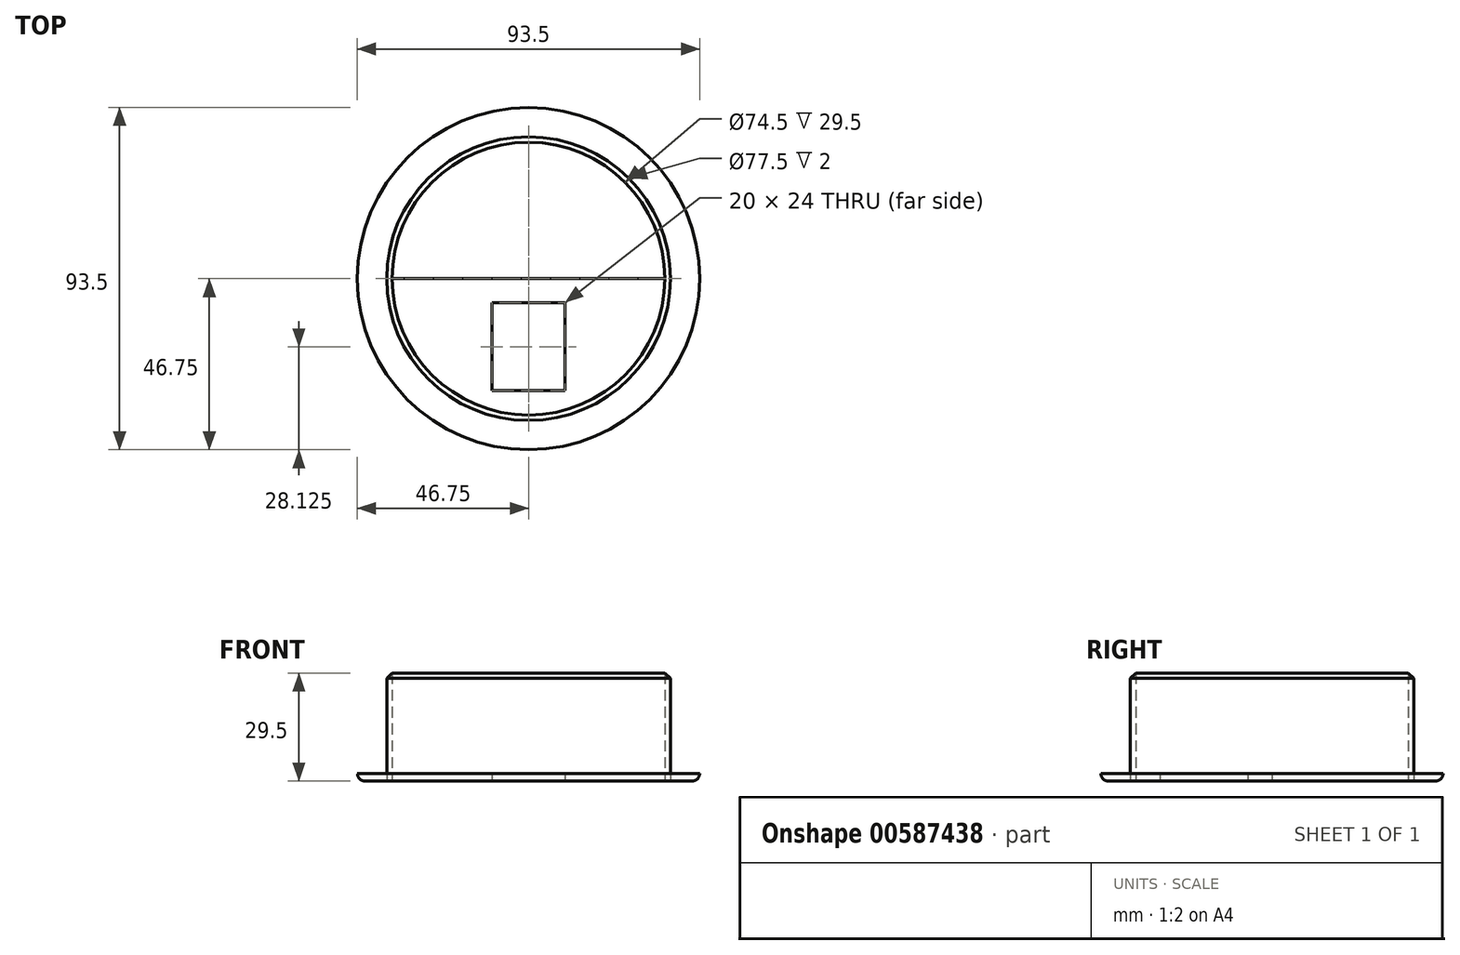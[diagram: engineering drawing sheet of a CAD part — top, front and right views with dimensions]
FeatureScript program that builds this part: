
annotation { "Feature Type Name" : "Feature", "Feature Type Description" : "" }
export const myFeature = defineFeature(function(context is Context, id is Id, definition is map)
    precondition{}
    {
        {
            var Q0;
            Q0=qCreatedBy(makeId("Top.planeOp"),FACE);
            var sketch = newSketch(context, id + "F0", { "sketchPlane" : qUnion([Q0])});
            skCircle(sketch, "E0", {"center": v(0, 0) * mm, "radius": 46.75 * mm});
            skCircle(sketch, "E1", {"center": v(0, 0) * mm, "radius": 38.75 * mm});
            skCircle(sketch, "E2", {"center": v(0, 0) * mm, "radius": 37.25 * mm});
            skLineSegment(sketch, "E3", {"start": v(37.25, 0) * mm, "end": v(38.75, 0) * mm, "construction": true});
            skLineSegment(sketch, "E4", {"start": v(38.75, 0) * mm, "end": v(46.75, 0) * mm, "construction": true});
            skLineSegment(sketch, "E5", {"start": v(-37.25, 0) * mm, "end": v(37.25, 0) * mm});
            skLineSegment(sketch, "E6.bottom", {"start": v(-10, -6.62) * mm, "end": v(10, -6.62) * mm});
            skLineSegment(sketch, "E6.top", {"start": v(-10, -30.62) * mm, "end": v(10, -30.62) * mm});
            skLineSegment(sketch, "E6.left", {"start": v(-10, -6.63) * mm, "end": v(-10, -30.62) * mm});
            skLineSegment(sketch, "E6.right", {"start": v(10, -6.63) * mm, "end": v(10, -30.62) * mm});
            skLineSegment(sketch, "E7", {"start": v(0, -30.62) * mm, "end": v(0, -6.63) * mm, "construction": true});
            skPoint(sketch, "E8", {"position": v(0, -18.62) * mm});
            skLineSegment(sketch, "E9", {"start": v(0, 0) * mm, "end": v(0, -37.25) * mm, "construction": true});
            skSolve(sketch);
        }
        {
            var Q0;
            Q0=makeQuery(id+"F0.imprint","IMPRINT",FACE,{"disambiguationData":[TD([[makeQuery(id+"F0.imprint","IMPRINT",EDGE,{"derivedFrom":sQuery(id+"F0.wireOp",EDGE,"E0")}),1.0]])]});
            var Q1;
            {var subQ0=sQuery(id+"F0.wireOp",EDGE,"E5");Q1=makeQuery(id+"F0.imprint","IMPRINT",FACE,{"disambiguationData":[TD([[makeQuery(id+"F0.imprint","IMPRINT",EDGE,{"derivedFrom":subQ0}),-1.0]])]});}
            extrude(context, id + "F1", {"entities" : qUnion([Q0, Q1]), "depth" : 2 * mm, "offsetDistance" : 25 * mm});
        }
        {
            var Q0;
            Q0=makeQuery(id+"F0.imprint","IMPRINT",FACE,{"disambiguationData":[TD([[makeQuery(id+"F0.imprint","IMPRINT",EDGE,{"derivedFrom":sQuery(id+"F0.wireOp",EDGE,"E1")}),1.0]])]});
            extrude(context, id + "F2", {"entities" : qUnion([Q0]), "depth" : 30 * mm, "offsetDistance" : 25 * mm});
        }
        {
            var Q0;
            Q0=makeQuery(id+"F2.opExtrude","CAP_EDGE",EDGE,{"disambiguationData":[OSD([sQuery(id+"F0.wireOp",EDGE,"E1")])],"isStart":false});
            chamfer(context, id + "F3", {"entities" : qUnion([Q0]), "width" : 2 * mm, "tangentPropagation" : true});
        }
        {
            var Q0;
            Q0=makeQuery(id+"F1.opExtrude","CAP_EDGE",EDGE,{"disambiguationData":[OSD([sQuery(id+"F0.wireOp",EDGE,"E0")])],"isStart":true});
            fillet(context, id + "F4", {"entities" : qUnion([Q0]), "radius" : 2 * mm, "tangentPropagation" : true, "allowEdgeOverflow" : false});
        }
    });
